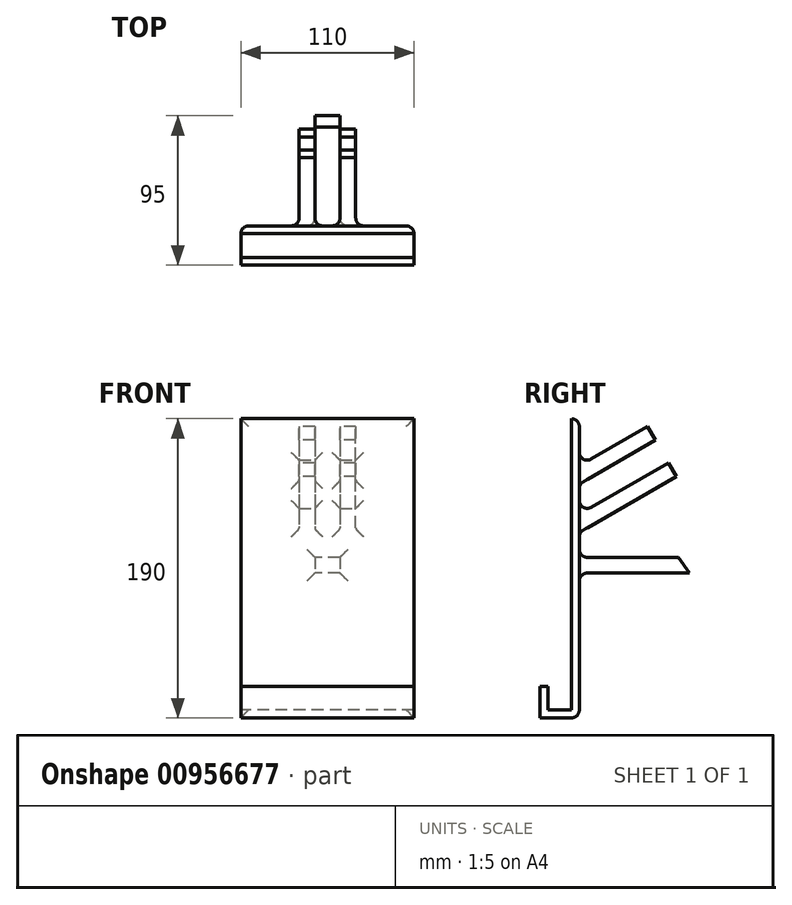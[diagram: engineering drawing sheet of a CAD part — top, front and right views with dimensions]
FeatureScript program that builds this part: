
annotation { "Feature Type Name" : "Feature", "Feature Type Description" : "" }
export const myFeature = defineFeature(function(context is Context, id is Id, definition is map)
    precondition{}
    {
        {
            var Q0;
            Q0=qCreatedBy(makeId("Right.planeOp"),FACE);
            var sketch = newSketch(context, id + "F0", { "sketchPlane" : qUnion([Q0])});
            skLineSegment(sketch, "E0.bottom", {"start": v(-5, 88.05) * mm, "end": v(0, 88.05) * mm});
            skLineSegment(sketch, "E0.top", {"start": v(-5, -101.95) * mm, "end": v(0, -101.95) * mm});
            skLineSegment(sketch, "E0.left", {"start": v(-5, 88.05) * mm, "end": v(-5, -101.95) * mm});
            skLineSegment(sketch, "E0.right", {"start": v(0, 88.05) * mm, "end": v(0, -101.95) * mm});
            skLineSegment(sketch, "E1.bottom", {"start": v(-5, -101.95) * mm, "end": v(-20, -101.95) * mm});
            skLineSegment(sketch, "E1.top", {"start": v(-5, -96.95) * mm, "end": v(-20, -96.95) * mm});
            skLineSegment(sketch, "E1.left", {"start": v(-5, -101.95) * mm, "end": v(-5, -96.95) * mm});
            skLineSegment(sketch, "E1.right", {"start": v(-20, -101.95) * mm, "end": v(-20, -96.95) * mm});
            skLineSegment(sketch, "E2.bottom", {"start": v(-25, -101.95) * mm, "end": v(-20, -101.95) * mm});
            skLineSegment(sketch, "E2.top", {"start": v(-25, -81.95) * mm, "end": v(-20, -81.95) * mm});
            skLineSegment(sketch, "E2.left", {"start": v(-25, -101.95) * mm, "end": v(-25, -81.95) * mm});
            skLineSegment(sketch, "E2.right", {"start": v(-20, -101.95) * mm, "end": v(-20, -81.95) * mm});
            skLineSegment(sketch, "E3.bottom", {"start": v(0, 58.05) * mm, "end": v(43.3, 83.05) * mm});
            skLineSegment(sketch, "E3.top", {"start": v(0, 46.5) * mm, "end": v(48.3, 74.4) * mm});
            skLineSegment(sketch, "E3.right", {"start": v(43.3, 83.05) * mm, "end": v(48.3, 74.4) * mm});
            skLineSegment(sketch, "E4.bottom", {"start": v(0, 27.45) * mm, "end": v(56.55, 60.1) * mm});
            skLineSegment(sketch, "E4.top", {"start": v(0, 15.9) * mm, "end": v(61.55, 51.44) * mm});
            skLineSegment(sketch, "E4.right", {"start": v(56.55, 60.1) * mm, "end": v(61.55, 51.44) * mm});
            skLineSegment(sketch, "E5.bottom", {"start": v(0, 0) * mm, "end": v(62.86, 0) * mm});
            skLineSegment(sketch, "E5.top", {"start": v(0, -10) * mm, "end": v(70, -10) * mm});
            skLineSegment(sketch, "E5.left", {"start": v(0, 0) * mm, "end": v(0, -10) * mm});
            skLineSegment(sketch, "E6", {"start": v(70, -10) * mm, "end": v(70, -10) * mm});
            skLineSegment(sketch, "E7", {"start": v(70, -10) * mm, "end": v(62.86, 0) * mm});
            skLineSegment(sketch, "E8", {"start": v(0, 88.05) * mm, "end": v(70, -10) * mm});
            skLineSegment(sketch, "E9", {"start": v(48.3, 74.4) * mm, "end": v(56.55, 60.1) * mm});
            skSolve(sketch);
        }
        {
            var Q0;
            {var subQ0=sQuery(id+"F0.wireOp",EDGE,"E4.right");var subQ1=sQuery(id+"F0.wireOp",EDGE,"E4.bottom");var subQ7=sQuery(id+"F0.wireOp",EDGE,"E0.right");var subQ8=makeQuery(id+"F0.imprint","INTERSECT",VERTEX,{"derivedFrom":[subQ7,subQ1]});Q0=qUnion([makeQuery(id+"F0.imprint","IMPRINT",FACE,{"disambiguationData":[TD([[makeQuery(id+"F0.imprint","IMPRINT",EDGE,{"disambiguationData":[TD([[subQ8,-1.0]])],"derivedFrom":subQ7}),1.0]])]}),makeQuery(id+"F0.imprint","IMPRINT",FACE,{"disambiguationData":[TD([[makeQuery(id+"F0.imprint","IMPRINT",EDGE,{"derivedFrom":subQ0}),-1.0]])]})]);}
            var Q1;
            {var subQ1=sQuery(id+"F0.wireOp",EDGE,"E3.bottom");var subQ3=sQuery(id+"F0.wireOp",EDGE,"E3.right");var subQ7=sQuery(id+"F0.wireOp",EDGE,"E0.right");var subQ8=makeQuery(id+"F0.imprint","INTERSECT",VERTEX,{"derivedFrom":[subQ7,subQ1]});Q1=qUnion([makeQuery(id+"F0.imprint","IMPRINT",FACE,{"disambiguationData":[TD([[makeQuery(id+"F0.imprint","IMPRINT",EDGE,{"disambiguationData":[TD([[subQ8,-1.0]])],"derivedFrom":subQ7}),1.0]])]}),makeQuery(id+"F0.imprint","IMPRINT",FACE,{"disambiguationData":[TD([[makeQuery(id+"F0.imprint","IMPRINT",EDGE,{"derivedFrom":subQ3}),-1.0]])]})]);}
            var Q2;
            Q2=makeQuery(id+"F0.imprint","IMPRINT",FACE,{"disambiguationData":[TD([[makeQuery(id+"F0.imprint","IMPRINT",EDGE,{"derivedFrom":sQuery(id+"F0.wireOp",EDGE,"E1.right")}),1.0]])]});
            var Q3;
            {var subQ0=sQuery(id+"F0.wireOp",EDGE,"E1.bottom");Q3=makeQuery(id+"F0.imprint","IMPRINT",FACE,{"disambiguationData":[TD([[makeQuery(id+"F0.imprint","IMPRINT",EDGE,{"derivedFrom":subQ0}),-1.0]])]});}
            var Q4;
            {var subQ6=sQuery(id+"F0.wireOp",EDGE,"E0.bottom");Q4=makeQuery(id+"F0.imprint","IMPRINT",FACE,{"disambiguationData":[TD([[makeQuery(id+"F0.imprint","IMPRINT",EDGE,{"derivedFrom":subQ6}),-1.0]])]});}
            var Q5;
            {var subQ2=sQuery(id+"F0.wireOp",EDGE,"E5.bottom");Q5=makeQuery(id+"F0.imprint","IMPRINT",FACE,{"disambiguationData":[TD([[makeQuery(id+"F0.imprint","IMPRINT",EDGE,{"derivedFrom":subQ2}),-1.0]])]});}
            extrude(context, id + "F1", {"entities" : qUnion([Q0, Q1, Q2, Q3, Q4, Q5]), "depth" : 110 * mm, "offsetDistance" : 25 * mm});
        }
        {
            var Q0;
            Q0=qCreatedBy(makeId("Front.planeOp"),FACE);
            var sketch = newSketch(context, id + "F2", { "sketchPlane" : qUnion([Q0])});
            skLineSegment(sketch, "E10.bottom", {"start": v(110, 114.11) * mm, "end": v(0, 114.11) * mm});
            skLineSegment(sketch, "E10.top", {"start": v(110, -75.89) * mm, "end": v(0, -75.89) * mm});
            skLineSegment(sketch, "E10.left", {"start": v(110, 114.11) * mm, "end": v(110, -75.89) * mm});
            skLineSegment(sketch, "E10.right", {"start": v(0, 114.11) * mm, "end": v(0, -75.89) * mm});
            skLineSegment(sketch, "E11", {"start": v(55, 114.11) * mm, "end": v(55, -75.89) * mm});
            skLineSegment(sketch, "E12", {"start": v(47, 114.11) * mm, "end": v(47, -75.89) * mm});
            skLineSegment(sketch, "E13", {"start": v(63, 114.11) * mm, "end": v(63, -75.89) * mm});
            skLineSegment(sketch, "E14", {"start": v(110, 15.28) * mm, "end": v(0, 15.28) * mm});
            skLineSegment(sketch, "E15", {"start": v(37, 114.11) * mm, "end": v(37, -75.89) * mm});
            skLineSegment(sketch, "E16", {"start": v(37, -75.89) * mm, "end": v(73, -75.89) * mm});
            skLineSegment(sketch, "E17", {"start": v(73, -75.89) * mm, "end": v(73, 114.11) * mm});
            skSolve(sketch);
        }
        {
            var Q0;
            {var subQ0=sQuery(id+"F2.wireOp",EDGE,"E12");var subQ1=sQuery(id+"F2.wireOp",EDGE,"E10.bottom");var subQ2=makeQuery(id+"F2.imprint","INTERSECT",VERTEX,{"derivedFrom":[subQ1,subQ0]});Q0=makeQuery(id+"F2.imprint","IMPRINT",FACE,{"disambiguationData":[TD([[makeQuery(id+"F2.imprint","IMPRINT",EDGE,{"disambiguationData":[TD([[subQ2,1.0]])],"derivedFrom":subQ1}),1.0]])]});}
            var Q1;
            {var subQ0=sQuery(id+"F2.wireOp",EDGE,"E11");var subQ1=sQuery(id+"F2.wireOp",EDGE,"E10.bottom");var subQ2=makeQuery(id+"F2.imprint","INTERSECT",VERTEX,{"derivedFrom":[subQ1,subQ0]});Q1=makeQuery(id+"F2.imprint","IMPRINT",FACE,{"disambiguationData":[TD([[makeQuery(id+"F2.imprint","IMPRINT",EDGE,{"disambiguationData":[TD([[subQ2,1.0]])],"derivedFrom":subQ1}),1.0]])]});}
            var Q2;
            {var subQ0=sQuery(id+"F2.wireOp",EDGE,"E10.left");var subQ1=sQuery(id+"F2.wireOp",EDGE,"E10.top");var subQ2=makeQuery(id+"F2.imprint","INTERSECT",VERTEX,{"derivedFrom":[subQ1,subQ0]});Q2=makeQuery(id+"F2.imprint","IMPRINT",FACE,{"disambiguationData":[TD([[makeQuery(id+"F2.imprint","IMPRINT",EDGE,{"disambiguationData":[TD([[subQ2,-1.0]])],"derivedFrom":subQ1}),-1.0]])]});}
            var Q3;
            {var subQ0=sQuery(id+"F2.wireOp",EDGE,"E10.right");var subQ1=sQuery(id+"F2.wireOp",EDGE,"E10.top");var subQ2=makeQuery(id+"F2.imprint","INTERSECT",VERTEX,{"derivedFrom":[subQ1,subQ0]});Q3=makeQuery(id+"F2.imprint","IMPRINT",FACE,{"disambiguationData":[TD([[makeQuery(id+"F2.imprint","IMPRINT",EDGE,{"disambiguationData":[TD([[subQ2,1.0]])],"derivedFrom":subQ1}),-1.0]])]});}
            var Q4;
            {var subQ0=sQuery(id+"F2.wireOp",EDGE,"E12");var subQ1=sQuery(id+"F2.wireOp",EDGE,"E10.top");var subQ2=makeQuery(id+"F2.imprint","INTERSECT",VERTEX,{"derivedFrom":[subQ1,subQ0]});Q4=makeQuery(id+"F2.imprint","IMPRINT",FACE,{"disambiguationData":[TD([[makeQuery(id+"F2.imprint","IMPRINT",EDGE,{"disambiguationData":[TD([[subQ2,-1.0]])],"derivedFrom":subQ1}),-1.0]])]});}
            var Q5;
            {var subQ0=sQuery(id+"F2.wireOp",EDGE,"E13");var subQ1=sQuery(id+"F2.wireOp",EDGE,"E10.top");var subQ2=makeQuery(id+"F2.imprint","INTERSECT",VERTEX,{"derivedFrom":[subQ1,subQ0]});Q5=makeQuery(id+"F2.imprint","IMPRINT",FACE,{"disambiguationData":[TD([[makeQuery(id+"F2.imprint","IMPRINT",EDGE,{"disambiguationData":[TD([[subQ2,1.0]])],"derivedFrom":subQ1}),-1.0]])]});}
            var Q6;
            {var subQ0=sQuery(id+"F2.wireOp",EDGE,"E10.left");var subQ1=sQuery(id+"F2.wireOp",EDGE,"E10.bottom");var subQ2=makeQuery(id+"F2.imprint","INTERSECT",VERTEX,{"derivedFrom":[subQ1,subQ0]});Q6=makeQuery(id+"F2.imprint","IMPRINT",FACE,{"disambiguationData":[TD([[makeQuery(id+"F2.imprint","IMPRINT",EDGE,{"disambiguationData":[TD([[subQ2,-1.0]])],"derivedFrom":subQ1}),1.0]])]});}
            var Q7;
            {var subQ0=sQuery(id+"F2.wireOp",EDGE,"E15");var subQ1=sQuery(id+"F2.wireOp",EDGE,"E10.bottom");var subQ2=makeQuery(id+"F2.imprint","INTERSECT",VERTEX,{"derivedFrom":[subQ1,subQ0]});Q7=makeQuery(id+"F2.imprint","IMPRINT",FACE,{"disambiguationData":[TD([[makeQuery(id+"F2.imprint","IMPRINT",EDGE,{"disambiguationData":[TD([[subQ2,-1.0]])],"derivedFrom":subQ1}),1.0]])]});}
            extrude(context, id + "F3", {"entities" : qUnion([Q0, Q1, Q2, Q3, Q4, Q5, Q6, Q7]), "operationType" : NewBodyOperationType.REMOVE, "oppositeDirection" : true, "depth" : 100 * mm, "offsetDistance" : 25 * mm});
        }
        {
            var Q0;
            {var subQ0=sQuery(id+"F0.wireOp",EDGE,"E4.top");var subQ1=sQuery(id+"F0.wireOp",EDGE,"E0.right");var subQ6=sQuery(id+"F2.wireOp",EDGE,"E17");Q0=makeQuery(id+"F3.boolean.opBoolean","SPLIT",EDGE,{"disambiguationData":[TD([makeQuery(id+"F3.opExtrude","SWEPT_FACE",FACE,{"disambiguationData":[OSD([subQ6])]})])],"derivedFrom":makeQuery(id+"F1.opExtrude","SWEPT_EDGE",EDGE,{"disambiguationData":[OSD([subQ1,subQ0])]})});}
            var Q1;
            {var subQ0=sQuery(id+"F0.wireOp",EDGE,"E4.top");var subQ1=sQuery(id+"F0.wireOp",EDGE,"E0.right");var subQ7=sQuery(id+"F2.wireOp",EDGE,"E15");Q1=makeQuery(id+"F3.boolean.opBoolean","SPLIT",EDGE,{"disambiguationData":[TD([makeQuery(id+"F3.opExtrude","SWEPT_FACE",FACE,{"disambiguationData":[OSD([subQ7])]})])],"derivedFrom":makeQuery(id+"F1.opExtrude","SWEPT_EDGE",EDGE,{"disambiguationData":[OSD([subQ1,subQ0])]})});}
            var Q2;
            {var subQ0=sQuery(id+"F0.wireOp",EDGE,"E0.right");var subQ5=sQuery(id+"F0.wireOp",EDGE,"E3.top");var subQ6=sQuery(id+"F2.wireOp",EDGE,"E17");Q2=makeQuery(id+"F3.boolean.opBoolean","SPLIT",EDGE,{"disambiguationData":[TD([makeQuery(id+"F3.opExtrude","SWEPT_FACE",FACE,{"disambiguationData":[OSD([subQ6])]})])],"derivedFrom":makeQuery(id+"F1.opExtrude","SWEPT_EDGE",EDGE,{"disambiguationData":[OSD([subQ0,subQ5])]})});}
            var Q3;
            {var subQ6=sQuery(id+"F0.wireOp",EDGE,"E4.bottom");var subQ7=sQuery(id+"F2.wireOp",EDGE,"E17");Q3=makeQuery(id+"F3.boolean.opBoolean","COPY",EDGE,{"disambiguationData":[TD([makeQuery(id+"F1.opExtrude","SWEPT_FACE",FACE,{"disambiguationData":[OSD([subQ6])]})])],"derivedFrom":makeQuery(id+"F3.opExtrude","CAP_EDGE",EDGE,{"disambiguationData":[OSD([subQ7])],"isStart":true})});}
            var Q4;
            {var subQ0=sQuery(id+"F0.wireOp",EDGE,"E0.right");var subQ5=sQuery(id+"F0.wireOp",EDGE,"E4.bottom");var subQ6=sQuery(id+"F2.wireOp",EDGE,"E17");Q4=makeQuery(id+"F3.boolean.opBoolean","SPLIT",EDGE,{"disambiguationData":[TD([makeQuery(id+"F3.opExtrude","SWEPT_FACE",FACE,{"disambiguationData":[OSD([subQ6])]})])],"derivedFrom":makeQuery(id+"F1.opExtrude","SWEPT_EDGE",EDGE,{"disambiguationData":[OSD([subQ0,subQ5])]})});}
            var Q5;
            {var subQ3=sQuery(id+"F2.wireOp",EDGE,"E13");var subQ5=sQuery(id+"F2.wireOp",EDGE,"E10.bottom");var subQ6=sQuery(id+"F0.wireOp",EDGE,"E4.bottom");var subQ8=makeQuery(id+"F2.imprint","IMPRINT",EDGE,{"disambiguationData":[TD([[makeQuery(id+"F2.imprint","INTERSECT",VERTEX,{"derivedFrom":[subQ5,subQ3]}),-1.0]])],"derivedFrom":subQ3});Q5=makeQuery(id+"F3.boolean.opBoolean","COPY",EDGE,{"disambiguationData":[TD([makeQuery(id+"F1.opExtrude","SWEPT_FACE",FACE,{"disambiguationData":[OSD([subQ6])]})])],"derivedFrom":makeQuery(id+"F3.opExtrude","CAP_EDGE",EDGE,{"disambiguationData":[OSD([subQ3]),TDD([subQ8])],"isStart":true})});}
            var Q6;
            {var subQ0=sQuery(id+"F0.wireOp",EDGE,"E0.right");var subQ5=sQuery(id+"F0.wireOp",EDGE,"E4.bottom");var subQ7=sQuery(id+"F2.wireOp",EDGE,"E15");Q6=makeQuery(id+"F3.boolean.opBoolean","SPLIT",EDGE,{"disambiguationData":[TD([makeQuery(id+"F3.opExtrude","SWEPT_FACE",FACE,{"disambiguationData":[OSD([subQ7])]})])],"derivedFrom":makeQuery(id+"F1.opExtrude","SWEPT_EDGE",EDGE,{"disambiguationData":[OSD([subQ0,subQ5])]})});}
            var Q7;
            {var subQ6=sQuery(id+"F0.wireOp",EDGE,"E4.bottom");var subQ8=sQuery(id+"F2.wireOp",EDGE,"E15");Q7=makeQuery(id+"F3.boolean.opBoolean","COPY",EDGE,{"disambiguationData":[TD([makeQuery(id+"F1.opExtrude","SWEPT_FACE",FACE,{"disambiguationData":[OSD([subQ6])]})])],"derivedFrom":makeQuery(id+"F3.opExtrude","CAP_EDGE",EDGE,{"disambiguationData":[OSD([subQ8])],"isStart":true})});}
            var Q8;
            {var subQ4=sQuery(id+"F2.wireOp",EDGE,"E12");var subQ5=sQuery(id+"F2.wireOp",EDGE,"E10.bottom");var subQ6=sQuery(id+"F0.wireOp",EDGE,"E4.bottom");var subQ8=makeQuery(id+"F2.imprint","IMPRINT",EDGE,{"disambiguationData":[TD([[makeQuery(id+"F2.imprint","INTERSECT",VERTEX,{"derivedFrom":[subQ5,subQ4]}),-1.0]])],"derivedFrom":subQ4});Q8=makeQuery(id+"F3.boolean.opBoolean","COPY",EDGE,{"disambiguationData":[TD([makeQuery(id+"F1.opExtrude","SWEPT_FACE",FACE,{"disambiguationData":[OSD([subQ6])]})])],"derivedFrom":makeQuery(id+"F3.opExtrude","CAP_EDGE",EDGE,{"disambiguationData":[OSD([subQ4]),TDD([subQ8])],"isStart":true})});}
            var Q9;
            {var subQ6=sQuery(id+"F0.wireOp",EDGE,"E3.bottom");var subQ8=sQuery(id+"F2.wireOp",EDGE,"E15");Q9=makeQuery(id+"F3.boolean.opBoolean","COPY",EDGE,{"disambiguationData":[TD([makeQuery(id+"F1.opExtrude","SWEPT_FACE",FACE,{"disambiguationData":[OSD([subQ6])]})])],"derivedFrom":makeQuery(id+"F3.opExtrude","CAP_EDGE",EDGE,{"disambiguationData":[OSD([subQ8])],"isStart":true})});}
            var Q10;
            {var subQ6=sQuery(id+"F0.wireOp",EDGE,"E3.bottom");var subQ7=sQuery(id+"F2.wireOp",EDGE,"E17");Q10=makeQuery(id+"F3.boolean.opBoolean","COPY",EDGE,{"disambiguationData":[TD([makeQuery(id+"F1.opExtrude","SWEPT_FACE",FACE,{"disambiguationData":[OSD([subQ6])]})])],"derivedFrom":makeQuery(id+"F3.opExtrude","CAP_EDGE",EDGE,{"disambiguationData":[OSD([subQ7])],"isStart":true})});}
            var Q11;
            {var subQ0=sQuery(id+"F0.wireOp",EDGE,"E0.right");var subQ5=sQuery(id+"F0.wireOp",EDGE,"E3.bottom");var subQ6=sQuery(id+"F2.wireOp",EDGE,"E17");Q11=makeQuery(id+"F3.boolean.opBoolean","SPLIT",EDGE,{"disambiguationData":[TD([makeQuery(id+"F3.opExtrude","SWEPT_FACE",FACE,{"disambiguationData":[OSD([subQ6])]})])],"derivedFrom":makeQuery(id+"F1.opExtrude","SWEPT_EDGE",EDGE,{"disambiguationData":[OSD([subQ0,subQ5])]})});}
            var Q12;
            {var subQ2=sQuery(id+"F2.wireOp",EDGE,"E13");var subQ4=sQuery(id+"F2.wireOp",EDGE,"E10.bottom");var subQ6=sQuery(id+"F0.wireOp",EDGE,"E3.bottom");var subQ8=makeQuery(id+"F2.imprint","IMPRINT",EDGE,{"disambiguationData":[TD([[makeQuery(id+"F2.imprint","INTERSECT",VERTEX,{"derivedFrom":[subQ4,subQ2]}),-1.0]])],"derivedFrom":subQ2});Q12=makeQuery(id+"F3.boolean.opBoolean","COPY",EDGE,{"disambiguationData":[TD([makeQuery(id+"F1.opExtrude","SWEPT_FACE",FACE,{"disambiguationData":[OSD([subQ6])]})])],"derivedFrom":makeQuery(id+"F3.opExtrude","CAP_EDGE",EDGE,{"disambiguationData":[OSD([subQ2]),TDD([subQ8])],"isStart":true})});}
            var Q13;
            {var subQ0=sQuery(id+"F0.wireOp",EDGE,"E0.right");var subQ5=sQuery(id+"F0.wireOp",EDGE,"E3.top");var subQ7=sQuery(id+"F2.wireOp",EDGE,"E15");Q13=makeQuery(id+"F3.boolean.opBoolean","SPLIT",EDGE,{"disambiguationData":[TD([makeQuery(id+"F3.opExtrude","SWEPT_FACE",FACE,{"disambiguationData":[OSD([subQ7])]})])],"derivedFrom":makeQuery(id+"F1.opExtrude","SWEPT_EDGE",EDGE,{"disambiguationData":[OSD([subQ0,subQ5])]})});}
            var Q14;
            {var subQ0=sQuery(id+"F0.wireOp",EDGE,"E0.right");var subQ5=sQuery(id+"F0.wireOp",EDGE,"E3.bottom");var subQ7=sQuery(id+"F2.wireOp",EDGE,"E15");Q14=makeQuery(id+"F3.boolean.opBoolean","SPLIT",EDGE,{"disambiguationData":[TD([makeQuery(id+"F3.opExtrude","SWEPT_FACE",FACE,{"disambiguationData":[OSD([subQ7])]})])],"derivedFrom":makeQuery(id+"F1.opExtrude","SWEPT_EDGE",EDGE,{"disambiguationData":[OSD([subQ0,subQ5])]})});}
            var Q15;
            {var subQ3=sQuery(id+"F2.wireOp",EDGE,"E12");var subQ4=sQuery(id+"F2.wireOp",EDGE,"E10.bottom");var subQ6=sQuery(id+"F0.wireOp",EDGE,"E3.bottom");var subQ8=makeQuery(id+"F2.imprint","IMPRINT",EDGE,{"disambiguationData":[TD([[makeQuery(id+"F2.imprint","INTERSECT",VERTEX,{"derivedFrom":[subQ4,subQ3]}),-1.0]])],"derivedFrom":subQ3});Q15=makeQuery(id+"F3.boolean.opBoolean","COPY",EDGE,{"disambiguationData":[TD([makeQuery(id+"F1.opExtrude","SWEPT_FACE",FACE,{"disambiguationData":[OSD([subQ6])]})])],"derivedFrom":makeQuery(id+"F3.opExtrude","CAP_EDGE",EDGE,{"disambiguationData":[OSD([subQ3]),TDD([subQ8])],"isStart":true})});}
            var Q16;
            {var subQ0=sQuery(id+"F2.wireOp",EDGE,"E14");var subQ1=sQuery(id+"F2.wireOp",EDGE,"E13");var subQ2=sQuery(id+"F2.wireOp",EDGE,"E12");var subQ3=sQuery(id+"F2.wireOp",EDGE,"E10.bottom");var subQ4=sQuery(id+"F2.wireOp",EDGE,"E10.top");var subQ5=sQuery(id+"F0.wireOp",EDGE,"E0.right");Q16=makeQuery(id+"F3.boolean.opBoolean","MERGE",FACE,{"derivedFrom":[makeQuery(id+"F1.opExtrude","SWEPT_FACE",FACE,{"disambiguationData":[OSD([subQ5]),TDD([makeQuery(id+"F0.imprint","IMPRINT",EDGE,{"disambiguationData":[TD([[makeQuery(id+"F0.imprint","INTERSECT",VERTEX,{"derivedFrom":[sQuery(id+"F0.wireOp",EDGE,"E0.top"),subQ5]}),1.0]])],"derivedFrom":subQ5})])]}),makeQuery(id+"F1.opExtrude","SWEPT_FACE",FACE,{"disambiguationData":[OSD([subQ5]),TDD([makeQuery(id+"F0.imprint","IMPRINT",EDGE,{"disambiguationData":[TD([[makeQuery(id+"F0.imprint","INTERSECT",VERTEX,{"derivedFrom":[subQ5,sQuery(id+"F0.wireOp",EDGE,"E3.bottom")]}),1.0]])],"derivedFrom":subQ5})])]}),makeQuery(id+"F1.opExtrude","SWEPT_FACE",FACE,{"disambiguationData":[OSD([subQ5]),TDD([makeQuery(id+"F0.imprint","IMPRINT",EDGE,{"disambiguationData":[TD([[makeQuery(id+"F0.imprint","INTERSECT",VERTEX,{"derivedFrom":[subQ5,sQuery(id+"F0.wireOp",EDGE,"E4.bottom")]}),1.0]])],"derivedFrom":subQ5})])]}),makeQuery(id+"F1.opExtrude","SWEPT_FACE",FACE,{"disambiguationData":[OSD([subQ5]),TDD([makeQuery(id+"F0.imprint","IMPRINT",EDGE,{"disambiguationData":[TD([[makeQuery(id+"F0.imprint","INTERSECT",VERTEX,{"derivedFrom":[subQ5,sQuery(id+"F0.wireOp",EDGE,"E4.top")]}),-1.0]])],"derivedFrom":subQ5})])]})],"fromTools":[makeQuery(id+"F3.opExtrude","CAP_FACE",FACE,{"disambiguationData":[OSD([subQ3,subQ4,sQuery(id+"F2.wireOp",EDGE,"E10.right"),subQ2,subQ0,sQuery(id+"F2.wireOp",EDGE,"E15")])],"isStart":true}),makeQuery(id+"F3.opExtrude","CAP_FACE",FACE,{"disambiguationData":[OSD([subQ3,subQ4,sQuery(id+"F2.wireOp",EDGE,"E10.left"),subQ1,subQ0,sQuery(id+"F2.wireOp",EDGE,"E17")])],"isStart":true}),makeQuery(id+"F3.opExtrude","CAP_FACE",FACE,{"disambiguationData":[OSD([subQ3,subQ2,subQ1,subQ0])],"isStart":true})]});}
            fillet(context, id + "F4", {"entities" : qUnion([Q0, Q1, Q2, Q3, Q4, Q5, Q6, Q7, Q8, Q9, Q10, Q11, Q12, Q13, Q14, Q15, Q16]), "radius" : 5 * mm, "tangentPropagation" : true, "allowEdgeOverflow" : false});
        }
    });
